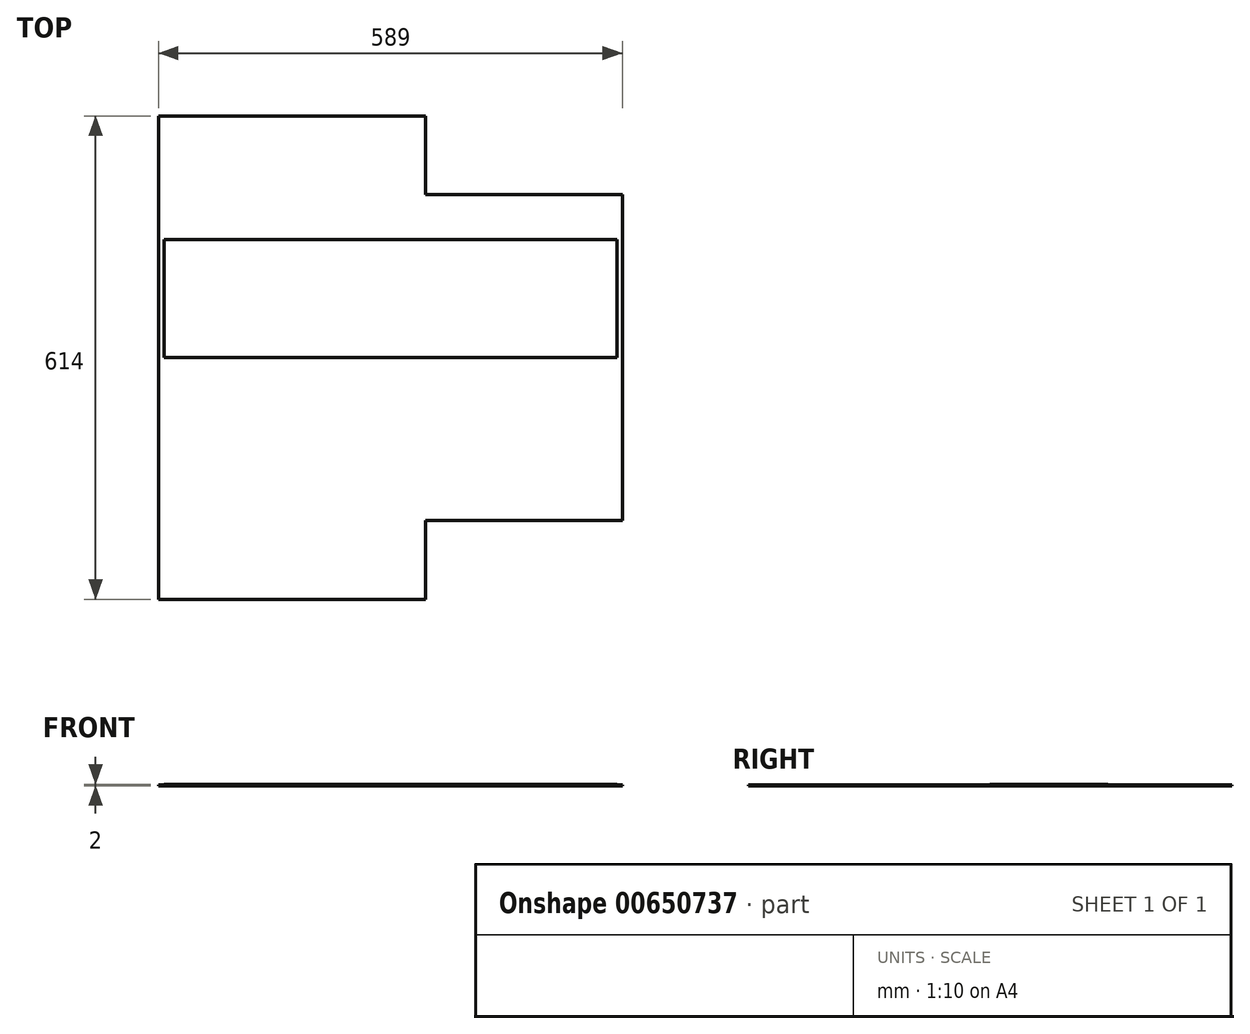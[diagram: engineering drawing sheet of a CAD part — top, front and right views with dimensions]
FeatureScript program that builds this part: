
annotation { "Feature Type Name" : "Feature", "Feature Type Description" : "" }
export const myFeature = defineFeature(function(context is Context, id is Id, definition is map)
    precondition{}
    {
        {
            var Q0;
            Q0=qCreatedBy(makeId("Top.planeOp"),FACE);
            var sketch = newSketch(context, id + "F0", { "sketchPlane" : qUnion([Q0])});
            skLineSegment(sketch, "E0.bottom", {"start": v(287.5, -100) * mm, "end": v(-287.5, -100) * mm, "construction": true});
            skLineSegment(sketch, "E0.left", {"start": v(287.5, -100) * mm, "end": v(287.5, 100) * mm, "construction": true});
            skLineSegment(sketch, "E0.right", {"start": v(-287.5, -100) * mm, "end": v(-287.5, 100) * mm, "construction": true});
            skPoint(sketch, "E0.middle", {"position": v(0, 0) * mm});
            skLineSegment(sketch, "E1.top", {"start": v(-287.5, 200) * mm, "end": v(37.5, 200) * mm, "construction": true});
            skLineSegment(sketch, "E1.left", {"start": v(-287.5, 100) * mm, "end": v(-287.5, 200) * mm, "construction": true});
            skLineSegment(sketch, "E1.right", {"start": v(37.5, 100) * mm, "end": v(37.5, 200) * mm, "construction": true});
            skLineSegment(sketch, "E2", {"start": v(37.5, 100) * mm, "end": v(287.5, 100) * mm, "construction": true});
            skLineSegment(sketch, "E3.MirrorCS", {"start": v(-287.5, -100) * mm, "end": v(-287.5, -300) * mm, "construction": true});
            skLineSegment(sketch, "E4.MirrorCS", {"start": v(-287.5, -300) * mm, "end": v(-287.5, -400) * mm, "construction": true});
            skLineSegment(sketch, "E5.MirrorCS", {"start": v(-287.5, -400) * mm, "end": v(37.5, -400) * mm, "construction": true});
            skLineSegment(sketch, "E6.MirrorCS", {"start": v(37.5, -300) * mm, "end": v(37.5, -400) * mm, "construction": true});
            skLineSegment(sketch, "E7.MirrorCS", {"start": v(37.5, -300) * mm, "end": v(287.5, -300) * mm, "construction": true});
            skLineSegment(sketch, "E8.MirrorCS", {"start": v(287.5, -100) * mm, "end": v(287.5, -300) * mm, "construction": true});
            skLineSegment(sketch, "E9.0", {"start": v(-294.5, -100) * mm, "end": v(-294.5, 100) * mm});
            skLineSegment(sketch, "E9.1", {"start": v(44.5, -307) * mm, "end": v(294.5, -307) * mm});
            skLineSegment(sketch, "E9.2", {"start": v(44.5, -307) * mm, "end": v(44.5, -407) * mm});
            skLineSegment(sketch, "E9.3", {"start": v(-294.5, -407) * mm, "end": v(44.5, -407) * mm});
            skLineSegment(sketch, "E9.4", {"start": v(-294.5, -300) * mm, "end": v(-294.5, -407) * mm});
            skLineSegment(sketch, "E9.5", {"start": v(294.5, -100) * mm, "end": v(294.5, -307) * mm});
            skLineSegment(sketch, "E9.6", {"start": v(-294.5, -100) * mm, "end": v(-294.5, -300) * mm});
            skLineSegment(sketch, "E9.7", {"start": v(294.5, -100) * mm, "end": v(294.5, 107) * mm});
            skLineSegment(sketch, "E9.8", {"start": v(44.5, 107) * mm, "end": v(294.5, 107) * mm});
            skLineSegment(sketch, "E9.9", {"start": v(44.5, 107) * mm, "end": v(44.5, 207) * mm});
            skLineSegment(sketch, "E9.10", {"start": v(-294.5, 207) * mm, "end": v(44.5, 207) * mm});
            skLineSegment(sketch, "E9.11", {"start": v(-294.5, 100) * mm, "end": v(-294.5, 207) * mm});
            skPoint(sketch, "E10.endSnap0", {"position": v(294.5, 3.5) * mm});
            skLineSegment(sketch, "E11", {"start": v(-287.5, 0) * mm, "end": v(287.5, 0) * mm, "construction": true});
            skLineSegment(sketch, "E12", {"start": v(162.51, 73) * mm, "end": v(162.51, 42) * mm});
            skLineSegment(sketch, "E13", {"start": v(162.51, 73) * mm, "end": v(262.51, 73) * mm});
            skLineSegment(sketch, "E14", {"start": v(262.51, 73) * mm, "end": v(262.51, 42) * mm});
            skLineSegment(sketch, "E15", {"start": v(262.51, 42) * mm, "end": v(162.51, 42) * mm});
            skLineSegment(sketch, "E16", {"start": v(162.51, 57.5) * mm, "end": v(262.51, 57.5) * mm, "construction": true});
            skLineSegment(sketch, "E17.MirrorCS", {"start": v(262.51, -42) * mm, "end": v(162.51, -42) * mm});
            skLineSegment(sketch, "E18.MirrorCS", {"start": v(162.51, -73) * mm, "end": v(162.51, -42) * mm});
            skLineSegment(sketch, "E19.MirrorCS", {"start": v(162.51, -73) * mm, "end": v(262.51, -73) * mm});
            skLineSegment(sketch, "E20.MirrorCS", {"start": v(262.51, -73) * mm, "end": v(262.51, -42) * mm});
            skSolve(sketch);
        }
        {
            var Q0;
            Q0=qCreatedBy(makeId("Top.planeOp"),FACE);
            var sketch = newSketch(context, id + "F1", { "sketchPlane" : qUnion([Q0])});
            skLineSegment(sketch, "E21.0", {"start": v(-287.5, 100) * mm, "end": v(-287.5, 200) * mm, "construction": true});
            skLineSegment(sketch, "E22.0", {"start": v(-287.5, -100) * mm, "end": v(-287.5, 100) * mm});
            skLineSegment(sketch, "E23.0", {"start": v(-287.5, 200) * mm, "end": v(37.5, 200) * mm, "construction": true});
            skLineSegment(sketch, "E24.0", {"start": v(37.5, 100) * mm, "end": v(37.5, 200) * mm, "construction": true});
            skLineSegment(sketch, "E25.0", {"start": v(37.5, 100) * mm, "end": v(287.5, 100) * mm, "construction": true});
            skLineSegment(sketch, "E26.0", {"start": v(287.5, -100) * mm, "end": v(287.5, 100) * mm, "construction": true});
            skLineSegment(sketch, "E27.0", {"start": v(287.5, -100) * mm, "end": v(-287.5, -100) * mm});
            skLineSegment(sketch, "E28", {"start": v(37.5, 100) * mm, "end": v(37.5, -100) * mm});
            skLineSegment(sketch, "E29", {"start": v(-287.5, 40) * mm, "end": v(37.5, 40) * mm, "construction": true});
            skLineSegment(sketch, "E30", {"start": v(-212.5, 40) * mm, "end": v(-212.5, -100) * mm, "construction": true});
            skLineSegment(sketch, "E31", {"start": v(-137.5, 40) * mm, "end": v(-137.5, -100) * mm, "construction": true});
            skLineSegment(sketch, "E32", {"start": v(-62.5, 40) * mm, "end": v(-62.5, -100) * mm, "construction": true});
            skLineSegment(sketch, "E33.0", {"start": v(-287.5, 50) * mm, "end": v(37.5, 50) * mm});
            skLineSegment(sketch, "E34", {"start": v(37.5, 50) * mm, "end": v(287.5, 50) * mm});
            skLineSegment(sketch, "E35", {"start": v(287.5, 50) * mm, "end": v(287.5, -100) * mm});
            skLineSegment(sketch, "E36", {"start": v(37.5, 40) * mm, "end": v(287.5, 40) * mm, "construction": true});
            skLineSegment(sketch, "E37", {"start": v(87.5, 40) * mm, "end": v(87.5, -74.83) * mm, "construction": true});
            skLineSegment(sketch, "E38", {"start": v(287.5, -100) * mm, "end": v(37.5, -100) * mm});
            skLineSegment(sketch, "E39", {"start": v(37.5, 50) * mm, "end": v(37.5, -100) * mm});
            skSolve(sketch);
        }
        {
            var Q0;
            Q0=makeQuery(id+"F0.imprint","IMPRINT",FACE,{"disambiguationData":[TD([[makeQuery(id+"F0.imprint","IMPRINT",EDGE,{"derivedFrom":sQuery(id+"F0.wireOp",EDGE,"E9.0")}),-1.0]])]});
            var Q1;
            Q1=makeQuery(id+"F0.imprint","IMPRINT",FACE,{"disambiguationData":[TD([[makeQuery(id+"F0.imprint","IMPRINT",EDGE,{"derivedFrom":sQuery(id+"F0.wireOp",EDGE,"E12")}),1.0]])]});
            var Q2;
            Q2=makeQuery(id+"F0.imprint","IMPRINT",FACE,{"disambiguationData":[TD([[makeQuery(id+"F0.imprint","IMPRINT",EDGE,{"derivedFrom":sQuery(id+"F0.wireOp",EDGE,"E17.MirrorCS")}),1.0]])]});
            var Q3;
            Q3=sQuery(id+"F0.wireOp",EDGE,"E9.11");
            var Q4;
            Q4=sQuery(id+"F0.wireOp",EDGE,"E9.10");
            var Q5;
            Q5=sQuery(id+"F0.wireOp",EDGE,"E9.9");
            var Q6;
            Q6=sQuery(id+"F0.wireOp",EDGE,"E9.8");
            var Q7;
            Q7=sQuery(id+"F0.wireOp",EDGE,"E9.7");
            var Q8;
            Q8=sQuery(id+"F0.wireOp",EDGE,"E9.5");
            var Q9;
            Q9=sQuery(id+"F0.wireOp",EDGE,"E9.1");
            var Q10;
            Q10=sQuery(id+"F0.wireOp",EDGE,"E9.2");
            var Q11;
            Q11=sQuery(id+"F0.wireOp",EDGE,"E9.3");
            var Q12;
            Q12=sQuery(id+"F0.wireOp",EDGE,"E9.4");
            var Q13;
            Q13=sQuery(id+"F0.wireOp",EDGE,"E9.6");
            var Q14;
            Q14=sQuery(id+"F0.wireOp",EDGE,"E9.0");
            extrude(context, id + "F2", {"entities" : qUnion([Q0, Q1, Q2]), "surfaceEntities" : qUnion([Q3, Q4, Q5, Q6, Q7, Q8, Q9, Q10, Q11, Q12, Q13, Q14]), "depth" : 1 * mm, "offsetDistance" : 25 * mm});
        }
        {
            var Q0;
            {var subQ3=sQuery(id+"F1.wireOp",EDGE,"E33.0");Q0=makeQuery(id+"F1.imprint","IMPRINT",FACE,{"disambiguationData":[TD([[makeQuery(id+"F1.imprint","IMPRINT",EDGE,{"derivedFrom":subQ3}),-1.0]])]});}
            var Q1;
            Q1=makeQuery(id+"F1.imprint","IMPRINT",FACE,{"disambiguationData":[TD([[makeQuery(id+"F1.imprint","IMPRINT",EDGE,{"derivedFrom":sQuery(id+"F1.wireOp",EDGE,"E35")}),-1.0]])]});
            extrude(context, id + "F3", {"entities" : qUnion([Q0, Q1]), "depth" : 2 * mm, "offsetDistance" : 25 * mm, "hasSecondDirection" : true, "secondDirectionOppositeDirection" : false, "secondDirectionDepth" : 1 * mm});
        }
    });
